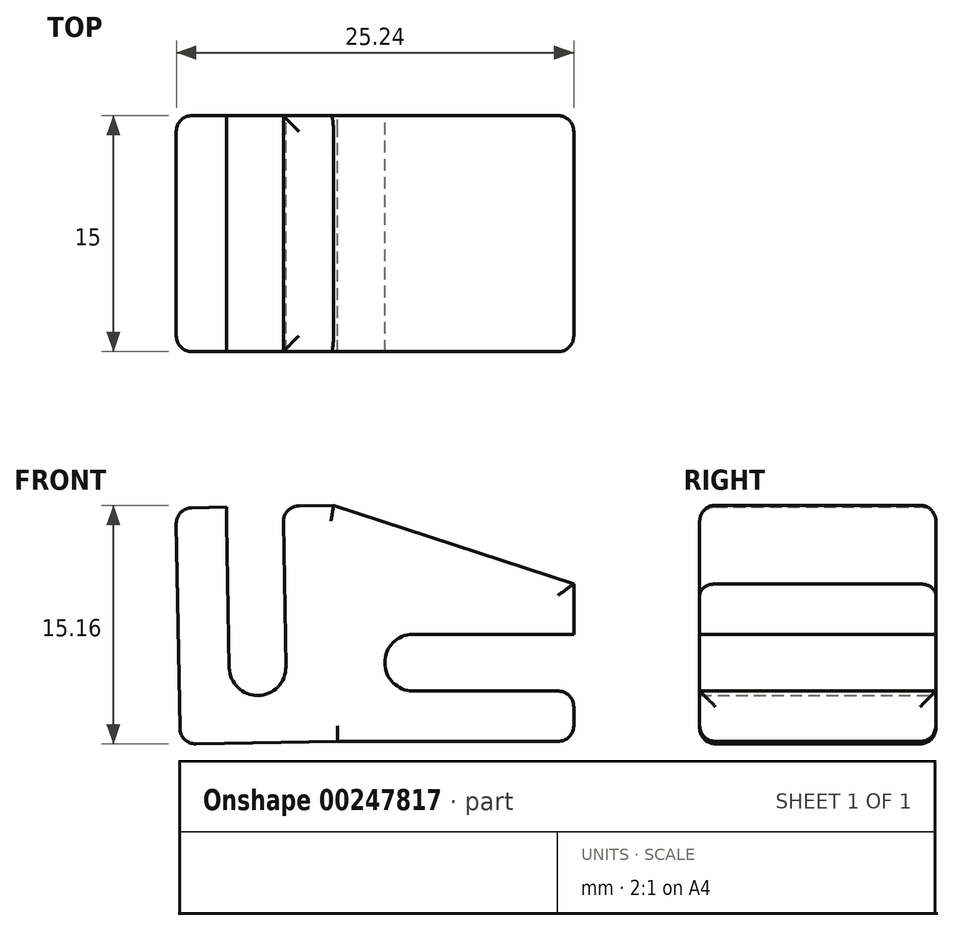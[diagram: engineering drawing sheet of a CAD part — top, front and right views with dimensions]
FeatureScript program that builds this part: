
annotation { "Feature Type Name" : "Feature", "Feature Type Description" : "" }
export const myFeature = defineFeature(function(context is Context, id is Id, definition is map)
    precondition{}
    {
        {
            var Q0;
            Q0=qCreatedBy(makeId("Top.planeOp"),FACE);
            var sketch = newSketch(context, id + "F0", { "sketchPlane" : qUnion([Q0])});
            skLineSegment(sketch, "E0.bottom", {"start": v(0, 0) * mm, "end": v(15, 0) * mm});
            skLineSegment(sketch, "E0.top", {"start": v(0, 15) * mm, "end": v(15, 15) * mm});
            skLineSegment(sketch, "E0.left", {"start": v(0, 0) * mm, "end": v(0, 15) * mm});
            skLineSegment(sketch, "E0.right", {"start": v(15, 0) * mm, "end": v(15, 15) * mm});
            skSolve(sketch);
        }
        {
            var Q0;
            Q0=makeQuery(id+"F0.imprint","IMPRINT",FACE,{"disambiguationData":[TD([[makeQuery(id+"F0.imprint","IMPRINT",EDGE,{"derivedFrom":sQuery(id+"F0.wireOp",EDGE,"E0.bottom")}),1.0]])]});
            extrude(context, id + "F1", {"entities" : qUnion([Q0]), "depth" : 10 * mm});
        }
        {
            var Q0;
            Q0=makeQuery(id+"F1.opExtrude","SWEPT_FACE",FACE,{"disambiguationData":[OSD([sQuery(id+"F0.wireOp",EDGE,"E0.right")])]});
            var sketch = newSketch(context, id + "F2", { "sketchPlane" : qUnion([Q0])});
            skLineSegment(sketch, "E1.bottom", {"start": v(0, 6.8) * mm, "end": v(15, 6.8) * mm});
            skLineSegment(sketch, "E1.top", {"start": v(0, 3.2) * mm, "end": v(15, 3.2) * mm});
            skLineSegment(sketch, "E1.left", {"start": v(0, 6.8) * mm, "end": v(0, 3.2) * mm});
            skLineSegment(sketch, "E1.right", {"start": v(15, 6.8) * mm, "end": v(15, 3.2) * mm});
            skSolve(sketch);
        }
        {
            var Q0;
            Q0=qSketchRegion(id+"F2",true);
            extrude(context, id + "F3", {"entities" : qUnion([Q0]), "operationType" : NewBodyOperationType.REMOVE, "oppositeDirection" : true, "depth" : 12 * mm});
        }
        {
            var Q0;
            Q0=makeQuery(id+"F3.boolean.opBoolean","COPY",EDGE,{"derivedFrom":makeQuery(id+"F3.opExtrude","CAP_EDGE",EDGE,{"disambiguationData":[OSD([sQuery(id+"F2.wireOp",EDGE,"E1.top")])],"isStart":false})});
            var Q1;
            Q1=makeQuery(id+"F3.boolean.opBoolean","COPY",EDGE,{"derivedFrom":makeQuery(id+"F3.opExtrude","CAP_EDGE",EDGE,{"disambiguationData":[OSD([sQuery(id+"F2.wireOp",EDGE,"E1.bottom")])],"isStart":false})});
            fillet(context, id + "F4", {"entities" : qUnion([Q0, Q1]), "radius" : 1.8 * mm, "tangentPropagation" : true, "allowEdgeOverflow" : false});
        }
        {
            var Q0;
            Q0=makeQuery(id+"F1.opExtrude","SWEPT_BODY",BODY,{"disambiguationData":[OSD([sQuery(id+"F0.wireOp",EDGE,"E0.bottom"),sQuery(id+"F0.wireOp",EDGE,"E0.top"),sQuery(id+"F0.wireOp",EDGE,"E0.left"),sQuery(id+"F0.wireOp",EDGE,"E0.right")])]});
            var Q1;
            Q1=makeQuery(id+"F1.opExtrude","CAP_EDGE",EDGE,{"disambiguationData":[OSD([sQuery(id+"F0.wireOp",EDGE,"E0.left")])],"isStart":true});
            circularPattern(context, id + "F5", {"entities" : qUnion([Q0]), "axis" : qUnion([Q1]), "angle" : 91 * degree, "instanceCount" : 2, "oppositeDirection" : true, "equalSpace" : true});
        }
        {
            var Q0;
            Q0=makeQuery(id+"F1.opExtrude","SWEPT_FACE",FACE,{"disambiguationData":[OSD([sQuery(id+"F0.wireOp",EDGE,"E0.bottom")])]});
            var sketch = newSketch(context, id + "F6", { "sketchPlane" : qUnion([Q0])});
            skLineSegment(sketch, "E2", {"start": v(0, 10) * mm, "end": v(-0.17, 10) * mm});
            skLineSegment(sketch, "E3", {"start": v(-0.17, 10) * mm, "end": v(0, 0) * mm});
            skLineSegment(sketch, "E4", {"start": v(0, 0) * mm, "end": v(0, 10) * mm});
            skSolve(sketch);
        }
        {
            var Q0;
            Q0 = qSketchRegion(id + "F6", true);
            var Q1;
            Q1=makeQuery(id+"F1.opExtrude","SWEPT_FACE",FACE,{"disambiguationData":[OSD([sQuery(id+"F0.wireOp",EDGE,"E0.top")])]});
            extrude(context, id + "F7", {"entities" : qUnion([Q0]), "operationType" : NewBodyOperationType.ADD, "endBound" : BoundingType.UP_TO_SURFACE, "oppositeDirection" : true, "endBoundEntityFace" : qUnion([Q1]), "depth" : 25 * mm});
        }
        {
            var Q0;
            Q0=qCreatedBy(makeId("Front.planeOp"),FACE);
            var sketch = newSketch(context, id + "F8", { "sketchPlane" : qUnion([Q0])});
            skLineSegment(sketch, "E5", {"start": v(-0.17, 10) * mm, "end": v(-0.26, 15) * mm});
            skLineSegment(sketch, "E6", {"start": v(-0.26, 15) * mm, "end": v(15, 10) * mm});
            skLineSegment(sketch, "E7", {"start": v(15, 10) * mm, "end": v(-0.17, 10) * mm});
            skSolve(sketch);
        }
        {
            var Q0;
            Q0 = qSketchRegion(id + "F8", true);
            var Q1;
            Q1=makeQuery(id+"F1.opExtrude","SWEPT_FACE",FACE,{"disambiguationData":[OSD([sQuery(id+"F0.wireOp",EDGE,"E0.top")])]});
            extrude(context, id + "F9", {"entities" : qUnion([Q0]), "operationType" : NewBodyOperationType.ADD, "endBound" : BoundingType.UP_TO_SURFACE, "oppositeDirection" : true, "endBoundEntityFace" : qUnion([Q1]), "depth" : 25 * mm});
        }
        {
            var Q0;
            Q0=makeQuery(id+"F3.boolean.opBoolean","COPY",EDGE,{"derivedFrom":makeQuery(id+"F3.opExtrude","SWEPT_EDGE",EDGE,{"disambiguationData":[OSD([sQuery(id+"F0.wireOp",EDGE,"E0.bottom"),sQuery(id+"F0.wireOp",EDGE,"E0.right"),sQuery(id+"F2.wireOp",EDGE,"E1.bottom"),sQuery(id+"F2.wireOp",EDGE,"E1.left")])]})});
            var Q1;
            Q1=makeQuery(id+"F3.boolean.opBoolean","COPY",EDGE,{"derivedFrom":makeQuery(id+"F3.opExtrude","CAP_EDGE",EDGE,{"disambiguationData":[OSD([sQuery(id+"F2.wireOp",EDGE,"E1.bottom")])],"isStart":true})});
            var Q2;
            {var subQ0=sQuery(id+"F0.wireOp",EDGE,"E0.right");var subQ1=sQuery(id+"F0.wireOp",EDGE,"E0.top");Q2=makeQuery(id+"F3.boolean.opBoolean","SPLIT",EDGE,{"disambiguationData":[TD([makeQuery(id+"F3.opExtrude","SWEPT_FACE",FACE,{"disambiguationData":[OSD([sQuery(id+"F2.wireOp",EDGE,"E1.top")])]})])],"derivedFrom":makeQuery(id+"F1.opExtrude","SWEPT_EDGE",EDGE,{"disambiguationData":[OSD([subQ1,subQ0])]})});}
            var Q3;
            {var subQ0=sQuery(id+"F0.wireOp",EDGE,"E0.bottom");var subQ1=sQuery(id+"F0.wireOp",EDGE,"E0.right");Q3=makeQuery(id+"F3.boolean.opBoolean","SPLIT",EDGE,{"disambiguationData":[TD([makeQuery(id+"F3.opExtrude","SWEPT_FACE",FACE,{"disambiguationData":[OSD([sQuery(id+"F2.wireOp",EDGE,"E1.top")])]})])],"derivedFrom":makeQuery(id+"F1.opExtrude","SWEPT_EDGE",EDGE,{"disambiguationData":[OSD([subQ0,subQ1])]})});}
            var Q4;
            Q4=makeQuery(id+"F3.boolean.opBoolean","COPY",EDGE,{"derivedFrom":makeQuery(id+"F3.opExtrude","CAP_EDGE",EDGE,{"disambiguationData":[OSD([sQuery(id+"F2.wireOp",EDGE,"E1.top")])],"isStart":true})});
            var Q5;
            Q5=makeQuery(id+"F3.boolean.opBoolean","COPY",EDGE,{"derivedFrom":makeQuery(id+"F3.opExtrude","SWEPT_EDGE",EDGE,{"disambiguationData":[OSD([sQuery(id+"F0.wireOp",EDGE,"E0.top"),sQuery(id+"F0.wireOp",EDGE,"E0.right"),sQuery(id+"F2.wireOp",EDGE,"E1.top"),sQuery(id+"F2.wireOp",EDGE,"E1.right")])]})});
            var Q6;
            Q6=makeQuery(id+"F1.opExtrude","CAP_EDGE",EDGE,{"disambiguationData":[OSD([sQuery(id+"F0.wireOp",EDGE,"E0.right")])],"isStart":true});
            var Q7;
            Q7=makeQuery(id+"F5.opPattern","COPY",EDGE,{"derivedFrom":makeQuery(id+"F1.opExtrude","CAP_EDGE",EDGE,{"disambiguationData":[OSD([sQuery(id+"F0.wireOp",EDGE,"E0.bottom")])],"isStart":false}),"instanceName":"1"});
            var Q8;
            Q8=makeQuery(id+"F5.opPattern","COPY",EDGE,{"derivedFrom":makeQuery(id+"F3.boolean.opBoolean","COPY",EDGE,{"derivedFrom":makeQuery(id+"F3.opExtrude","SWEPT_EDGE",EDGE,{"disambiguationData":[OSD([sQuery(id+"F0.wireOp",EDGE,"E0.bottom"),sQuery(id+"F0.wireOp",EDGE,"E0.right"),sQuery(id+"F2.wireOp",EDGE,"E1.bottom"),sQuery(id+"F2.wireOp",EDGE,"E1.left")])]})}),"instanceName":"1"});
            var Q9;
            {var subQ0=sQuery(id+"F0.wireOp",EDGE,"E0.bottom");var subQ1=sQuery(id+"F0.wireOp",EDGE,"E0.right");Q9=makeQuery(id+"F5.opPattern","COPY",EDGE,{"derivedFrom":makeQuery(id+"F3.boolean.opBoolean","SPLIT",EDGE,{"disambiguationData":[TD([makeQuery(id+"F3.opExtrude","SWEPT_FACE",FACE,{"disambiguationData":[OSD([sQuery(id+"F2.wireOp",EDGE,"E1.bottom")])]})])],"derivedFrom":makeQuery(id+"F1.opExtrude","SWEPT_EDGE",EDGE,{"disambiguationData":[OSD([subQ0,subQ1])]})}),"instanceName":"1"});}
            var Q10;
            Q10=makeQuery(id+"F5.opPattern","COPY",EDGE,{"derivedFrom":makeQuery(id+"F3.boolean.opBoolean","COPY",EDGE,{"derivedFrom":makeQuery(id+"F3.opExtrude","CAP_EDGE",EDGE,{"disambiguationData":[OSD([sQuery(id+"F2.wireOp",EDGE,"E1.bottom")])],"isStart":true})}),"instanceName":"1"});
            var Q11;
            {var subQ0=sQuery(id+"F0.wireOp",EDGE,"E0.right");var subQ1=sQuery(id+"F0.wireOp",EDGE,"E0.top");Q11=makeQuery(id+"F5.opPattern","COPY",EDGE,{"derivedFrom":makeQuery(id+"F3.boolean.opBoolean","SPLIT",EDGE,{"disambiguationData":[TD([makeQuery(id+"F3.opExtrude","SWEPT_FACE",FACE,{"disambiguationData":[OSD([sQuery(id+"F2.wireOp",EDGE,"E1.bottom")])]})])],"derivedFrom":makeQuery(id+"F1.opExtrude","SWEPT_EDGE",EDGE,{"disambiguationData":[OSD([subQ1,subQ0])]})}),"instanceName":"1"});}
            var Q12;
            Q12=makeQuery(id+"F5.opPattern","COPY",EDGE,{"derivedFrom":makeQuery(id+"F1.opExtrude","CAP_EDGE",EDGE,{"disambiguationData":[OSD([sQuery(id+"F0.wireOp",EDGE,"E0.right")])],"isStart":false}),"instanceName":"1"});
            var Q13;
            Q13=makeQuery(id+"F5.opPattern","COPY",EDGE,{"derivedFrom":makeQuery(id+"F1.opExtrude","CAP_EDGE",EDGE,{"disambiguationData":[OSD([sQuery(id+"F0.wireOp",EDGE,"E0.left")])],"isStart":false}),"instanceName":"1"});
            var Q14;
            Q14=makeQuery(id+"F5.opPattern","COPY",EDGE,{"derivedFrom":makeQuery(id+"F1.opExtrude","CAP_EDGE",EDGE,{"disambiguationData":[OSD([sQuery(id+"F0.wireOp",EDGE,"E0.top")])],"isStart":false}),"instanceName":"1"});
            var Q15;
            Q15=makeQuery(id+"F5.opPattern","COPY",EDGE,{"derivedFrom":makeQuery(id+"F3.boolean.opBoolean","COPY",EDGE,{"derivedFrom":makeQuery(id+"F3.opExtrude","CAP_EDGE",EDGE,{"disambiguationData":[OSD([sQuery(id+"F2.wireOp",EDGE,"E1.top")])],"isStart":true})}),"instanceName":"1"});
            var Q16;
            Q16=makeQuery(id+"F5.opPattern","COPY",EDGE,{"derivedFrom":makeQuery(id+"F1.opExtrude","SWEPT_EDGE",EDGE,{"disambiguationData":[OSD([sQuery(id+"F0.wireOp",EDGE,"E0.bottom"),sQuery(id+"F0.wireOp",EDGE,"E0.left")])]}),"instanceName":"1"});
            var Q17;
            Q17=makeQuery(id+"F1.opExtrude","CAP_EDGE",EDGE,{"disambiguationData":[OSD([sQuery(id+"F0.wireOp",EDGE,"E0.bottom")])],"isStart":true});
            var Q18;
            Q18=makeQuery(id+"F1.opExtrude","CAP_EDGE",EDGE,{"disambiguationData":[OSD([sQuery(id+"F0.wireOp",EDGE,"E0.top")])],"isStart":true});
            var Q19;
            Q19=makeQuery(id+"F5.opPattern","COPY",EDGE,{"derivedFrom":makeQuery(id+"F1.opExtrude","SWEPT_EDGE",EDGE,{"disambiguationData":[OSD([sQuery(id+"F0.wireOp",EDGE,"E0.top"),sQuery(id+"F0.wireOp",EDGE,"E0.left")])]}),"instanceName":"1"});
            var Q20;
            {var subQ0=sQuery(id+"F0.wireOp",EDGE,"E0.bottom");var subQ1=sQuery(id+"F0.wireOp",EDGE,"E0.right");Q20=makeQuery(id+"F3.boolean.opBoolean","SPLIT",EDGE,{"disambiguationData":[TD([makeQuery(id+"F3.opExtrude","SWEPT_FACE",FACE,{"disambiguationData":[OSD([sQuery(id+"F2.wireOp",EDGE,"E1.bottom")])]})])],"derivedFrom":makeQuery(id+"F1.opExtrude","SWEPT_EDGE",EDGE,{"disambiguationData":[OSD([subQ0,subQ1])]})});}
            var Q21;
            {var subQ0=sQuery(id+"F0.wireOp",EDGE,"E0.right");var subQ1=sQuery(id+"F0.wireOp",EDGE,"E0.top");Q21=makeQuery(id+"F3.boolean.opBoolean","SPLIT",EDGE,{"disambiguationData":[TD([makeQuery(id+"F3.opExtrude","SWEPT_FACE",FACE,{"disambiguationData":[OSD([sQuery(id+"F2.wireOp",EDGE,"E1.bottom")])]})])],"derivedFrom":makeQuery(id+"F1.opExtrude","SWEPT_EDGE",EDGE,{"disambiguationData":[OSD([subQ1,subQ0])]})});}
            var Q22;
            {var subQ0=sQuery(id+"F0.wireOp",EDGE,"E0.bottom");var subQ1=sQuery(id+"F0.wireOp",EDGE,"E0.right");Q22=makeQuery(id+"F5.opPattern","COPY",EDGE,{"derivedFrom":makeQuery(id+"F3.boolean.opBoolean","SPLIT",EDGE,{"disambiguationData":[TD([makeQuery(id+"F3.opExtrude","SWEPT_FACE",FACE,{"disambiguationData":[OSD([sQuery(id+"F2.wireOp",EDGE,"E1.top")])]})])],"derivedFrom":makeQuery(id+"F1.opExtrude","SWEPT_EDGE",EDGE,{"disambiguationData":[OSD([subQ0,subQ1])]})}),"instanceName":"1"});}
            var Q23;
            Q23=makeQuery(id+"F9.opExtrude","CAP_EDGE",EDGE,{"disambiguationData":[OSD([sQuery(id+"F8.wireOp",EDGE,"E6")])],"isStart":true});
            var Q24;
            {var subQ0=sQuery(id+"F0.wireOp",EDGE,"E0.right");var subQ1=sQuery(id+"F0.wireOp",EDGE,"E0.top");Q24=makeQuery(id+"F5.opPattern","COPY",EDGE,{"derivedFrom":makeQuery(id+"F3.boolean.opBoolean","SPLIT",EDGE,{"disambiguationData":[TD([makeQuery(id+"F3.opExtrude","SWEPT_FACE",FACE,{"disambiguationData":[OSD([sQuery(id+"F2.wireOp",EDGE,"E1.top")])]})])],"derivedFrom":makeQuery(id+"F1.opExtrude","SWEPT_EDGE",EDGE,{"disambiguationData":[OSD([subQ1,subQ0])]})}),"instanceName":"1"});}
            var Q25;
            Q25=makeQuery(id+"F9.opExtrude","CAP_EDGE",EDGE,{"disambiguationData":[OSD([sQuery(id+"F8.wireOp",EDGE,"E6")])],"isStart":false});
            fillet(context, id + "F10", {"entities" : qUnion([Q0, Q1, Q2, Q3, Q4, Q5, Q6, Q7, Q8, Q9, Q10, Q11, Q12, Q13, Q14, Q15, Q16, Q17, Q18, Q19, Q20, Q21, Q22, Q23, Q24, Q25]), "radius" : 1 * mm, "tangentPropagation" : true, "allowEdgeOverflow" : false});
        }
    });
